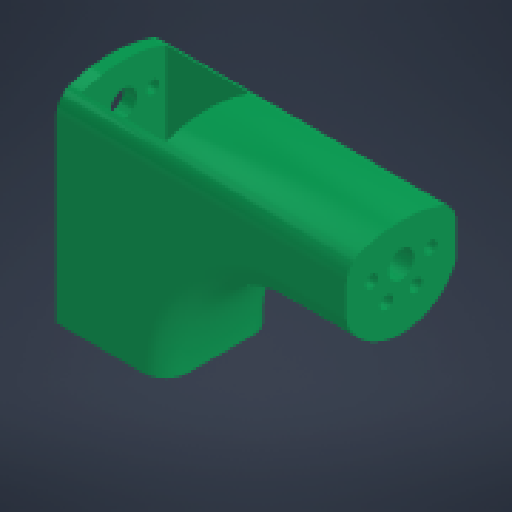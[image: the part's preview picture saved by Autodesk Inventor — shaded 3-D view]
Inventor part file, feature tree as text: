
AUTODESK INVENTOR PART (.ipt)
format: ipt  version: 2024 (Build 280153000, 153)  size: 348,672 bytes
history: native  units: mm
features: other x3, extrude x2, sketch x2, imported_body x1, fillet x1
ambient origin geometry x8: Origin, YZ Plane, XZ Plane, XY Plane, X Axis, Y Axis, Z Axis, Center Point
bodies: Body1 (feature_tree)
feature tree (9):
  other  "Твердое тело1"
  imported_body  "БазТело1"
  extrude  "Выдавливание1"  Depth=14.0mm
  extrude  "Выдавливание2"  Depth=3.0mm
  other  "Непосредственное редактирование2"
  fillet  "Сопряжение2"  Radius=9.0mm
  sketch  "Эскиз2"
  sketch  "Эскиз3"
  other  "Перенос2"
